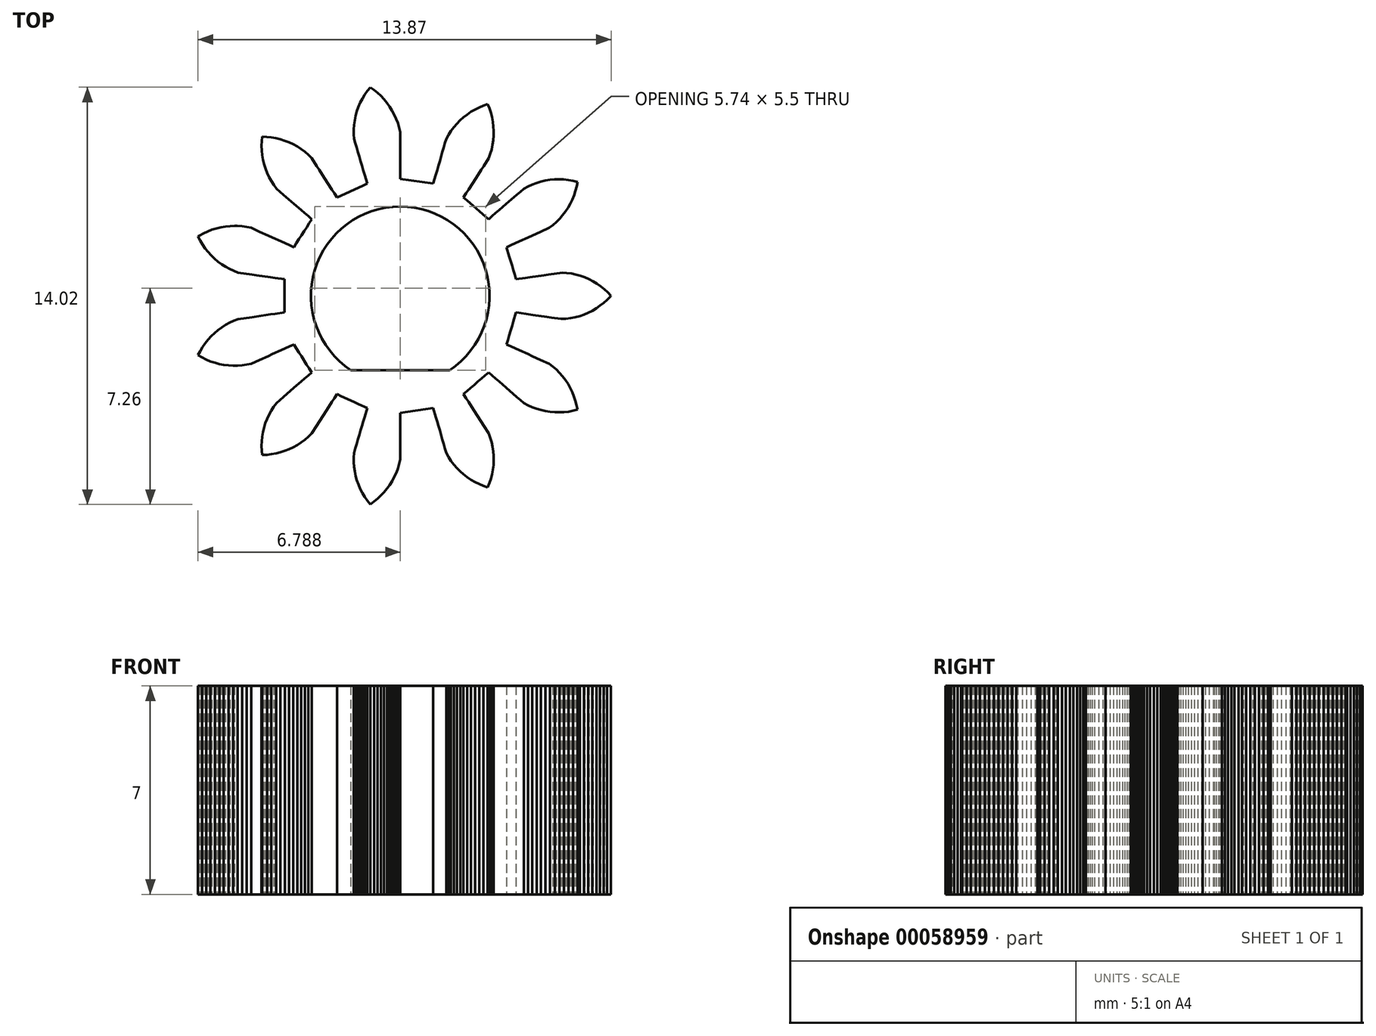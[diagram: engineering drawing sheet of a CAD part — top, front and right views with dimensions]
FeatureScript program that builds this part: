
annotation { "Feature Type Name" : "Feature", "Feature Type Description" : "" }
export const myFeature = defineFeature(function(context is Context, id is Id, definition is map)
    precondition{}
    {
        {
            var Q0;
            Q0=qCreatedBy(makeId("Top.planeOp"),FACE);
            var sketch = newSketch(context, id + "F0", { "sketchPlane" : qUnion([Q0])});
            skLineSegment(sketch, "E0", {"start": v(2.78, -0.56) * mm, "end": v(2.88, -0.57) * mm});
            skLineSegment(sketch, "E1", {"start": v(2.88, -0.57) * mm, "end": v(3.04, -0.6) * mm});
            skLineSegment(sketch, "E2", {"start": v(3.04, -0.6) * mm, "end": v(3.2, -0.62) * mm});
            skLineSegment(sketch, "E3", {"start": v(3.2, -0.62) * mm, "end": v(3.35, -0.64) * mm});
            skLineSegment(sketch, "E4", {"start": v(3.35, -0.64) * mm, "end": v(3.5, -0.66) * mm});
            skLineSegment(sketch, "E5", {"start": v(3.5, -0.66) * mm, "end": v(3.66, -0.69) * mm});
            skLineSegment(sketch, "E6", {"start": v(3.66, -0.69) * mm, "end": v(3.81, -0.7) * mm});
            skLineSegment(sketch, "E7", {"start": v(3.81, -0.7) * mm, "end": v(3.97, -0.73) * mm});
            skLineSegment(sketch, "E8", {"start": v(3.97, -0.73) * mm, "end": v(4.12, -0.75) * mm});
            skLineSegment(sketch, "E9", {"start": v(4.12, -0.75) * mm, "end": v(4.28, -0.78) * mm});
            skLineSegment(sketch, "E10", {"start": v(4.28, -0.78) * mm, "end": v(4.46, -0.77) * mm});
            skLineSegment(sketch, "E11", {"start": v(4.46, -0.77) * mm, "end": v(4.61, -0.75) * mm});
            skLineSegment(sketch, "E12", {"start": v(4.61, -0.75) * mm, "end": v(4.76, -0.72) * mm});
            skLineSegment(sketch, "E13", {"start": v(4.76, -0.72) * mm, "end": v(4.91, -0.68) * mm});
            skLineSegment(sketch, "E14", {"start": v(4.91, -0.68) * mm, "end": v(5.06, -0.63) * mm});
            skLineSegment(sketch, "E15", {"start": v(5.06, -0.63) * mm, "end": v(5.2, -0.57) * mm});
            skLineSegment(sketch, "E16", {"start": v(5.2, -0.57) * mm, "end": v(5.34, -0.5) * mm});
            skLineSegment(sketch, "E17", {"start": v(5.34, -0.5) * mm, "end": v(5.48, -0.42) * mm});
            skLineSegment(sketch, "E18", {"start": v(5.48, -0.42) * mm, "end": v(5.6, -0.33) * mm});
            skLineSegment(sketch, "E19", {"start": v(5.6, -0.33) * mm, "end": v(5.72, -0.23) * mm});
            skLineSegment(sketch, "E20", {"start": v(5.72, -0.23) * mm, "end": v(5.84, -0.13) * mm});
            skLineSegment(sketch, "E21", {"start": v(5.84, -0.13) * mm, "end": v(5.95, -0.02) * mm});
            skLineSegment(sketch, "E22", {"start": v(5.95, -0.02) * mm, "end": v(5.97, 0) * mm});
            skLineSegment(sketch, "E23", {"start": v(5.97, 0) * mm, "end": v(5.85, 0.12) * mm});
            skLineSegment(sketch, "E24", {"start": v(5.85, 0.12) * mm, "end": v(5.75, 0.22) * mm});
            skLineSegment(sketch, "E25", {"start": v(5.75, 0.22) * mm, "end": v(5.62, 0.32) * mm});
            skLineSegment(sketch, "E26", {"start": v(5.62, 0.32) * mm, "end": v(5.5, 0.4) * mm});
            skLineSegment(sketch, "E27", {"start": v(5.5, 0.4) * mm, "end": v(5.36, 0.49) * mm});
            skLineSegment(sketch, "E28", {"start": v(5.36, 0.49) * mm, "end": v(5.23, 0.56) * mm});
            skLineSegment(sketch, "E29", {"start": v(5.23, 0.56) * mm, "end": v(5.08, 0.62) * mm});
            skLineSegment(sketch, "E30", {"start": v(5.08, 0.62) * mm, "end": v(4.94, 0.67) * mm});
            skLineSegment(sketch, "E31", {"start": v(4.94, 0.67) * mm, "end": v(4.79, 0.72) * mm});
            skLineSegment(sketch, "E32", {"start": v(4.79, 0.72) * mm, "end": v(4.64, 0.75) * mm});
            skLineSegment(sketch, "E33", {"start": v(4.64, 0.75) * mm, "end": v(4.48, 0.77) * mm});
            skLineSegment(sketch, "E34", {"start": v(4.48, 0.77) * mm, "end": v(4.33, 0.78) * mm});
            skLineSegment(sketch, "E35", {"start": v(4.33, 0.78) * mm, "end": v(4.18, 0.76) * mm});
            skLineSegment(sketch, "E36", {"start": v(4.18, 0.76) * mm, "end": v(4.02, 0.74) * mm});
            skLineSegment(sketch, "E37", {"start": v(4.02, 0.74) * mm, "end": v(3.87, 0.72) * mm});
            skLineSegment(sketch, "E38", {"start": v(3.87, 0.72) * mm, "end": v(3.7, 0.7) * mm});
            skLineSegment(sketch, "E39", {"start": v(3.7, 0.7) * mm, "end": v(3.55, 0.67) * mm});
            skLineSegment(sketch, "E40", {"start": v(3.55, 0.67) * mm, "end": v(3.4, 0.65) * mm});
            skLineSegment(sketch, "E41", {"start": v(3.4, 0.65) * mm, "end": v(3.24, 0.63) * mm});
            skLineSegment(sketch, "E42", {"start": v(3.24, 0.63) * mm, "end": v(3.09, 0.6) * mm});
            skLineSegment(sketch, "E43", {"start": v(3.09, 0.6) * mm, "end": v(2.93, 0.58) * mm});
            skLineSegment(sketch, "E44", {"start": v(2.93, 0.58) * mm, "end": v(2.78, 0.56) * mm});
            skLineSegment(sketch, "E45", {"start": v(2.78, 0.56) * mm, "end": v(2.73, 0.71) * mm});
            skLineSegment(sketch, "E46", {"start": v(2.73, 0.71) * mm, "end": v(2.69, 0.87) * mm});
            skLineSegment(sketch, "E47", {"start": v(2.69, 0.87) * mm, "end": v(2.64, 1.02) * mm});
            skLineSegment(sketch, "E48", {"start": v(2.64, 1.02) * mm, "end": v(2.6, 1.17) * mm});
            skLineSegment(sketch, "E49", {"start": v(2.6, 1.17) * mm, "end": v(2.55, 1.33) * mm});
            skLineSegment(sketch, "E50", {"start": v(2.55, 1.33) * mm, "end": v(2.5, 1.48) * mm});
            skLineSegment(sketch, "E51", {"start": v(2.5, 1.48) * mm, "end": v(2.46, 1.63) * mm});
            skLineSegment(sketch, "E52", {"start": v(2.46, 1.63) * mm, "end": v(2.6, 1.7) * mm});
            skLineSegment(sketch, "E53", {"start": v(2.6, 1.7) * mm, "end": v(2.75, 1.76) * mm});
            skLineSegment(sketch, "E54", {"start": v(2.75, 1.76) * mm, "end": v(2.9, 1.83) * mm});
            skLineSegment(sketch, "E55", {"start": v(2.9, 1.83) * mm, "end": v(3.03, 1.9) * mm});
            skLineSegment(sketch, "E56", {"start": v(3.03, 1.9) * mm, "end": v(3.18, 1.96) * mm});
            skLineSegment(sketch, "E57", {"start": v(3.18, 1.96) * mm, "end": v(3.32, 2.02) * mm});
            skLineSegment(sketch, "E58", {"start": v(3.32, 2.02) * mm, "end": v(3.46, 2.09) * mm});
            skLineSegment(sketch, "E59", {"start": v(3.46, 2.09) * mm, "end": v(3.6, 2.15) * mm});
            skLineSegment(sketch, "E60", {"start": v(3.6, 2.15) * mm, "end": v(3.75, 2.22) * mm});
            skLineSegment(sketch, "E61", {"start": v(3.75, 2.22) * mm, "end": v(3.9, 2.28) * mm});
            skLineSegment(sketch, "E62", {"start": v(3.9, 2.28) * mm, "end": v(4.02, 2.38) * mm});
            skLineSegment(sketch, "E63", {"start": v(4.02, 2.38) * mm, "end": v(4.13, 2.48) * mm});
            skLineSegment(sketch, "E64", {"start": v(4.13, 2.48) * mm, "end": v(4.24, 2.6) * mm});
            skLineSegment(sketch, "E65", {"start": v(4.24, 2.6) * mm, "end": v(4.34, 2.7) * mm});
            skLineSegment(sketch, "E66", {"start": v(4.34, 2.7) * mm, "end": v(4.44, 2.83) * mm});
            skLineSegment(sketch, "E67", {"start": v(4.44, 2.83) * mm, "end": v(4.52, 2.96) * mm});
            skLineSegment(sketch, "E68", {"start": v(4.52, 2.96) * mm, "end": v(4.6, 3.1) * mm});
            skLineSegment(sketch, "E69", {"start": v(4.6, 3.1) * mm, "end": v(4.67, 3.23) * mm});
            skLineSegment(sketch, "E70", {"start": v(4.67, 3.23) * mm, "end": v(4.73, 3.38) * mm});
            skLineSegment(sketch, "E71", {"start": v(4.73, 3.38) * mm, "end": v(4.77, 3.52) * mm});
            skLineSegment(sketch, "E72", {"start": v(4.77, 3.52) * mm, "end": v(4.81, 3.68) * mm});
            skLineSegment(sketch, "E73", {"start": v(4.81, 3.68) * mm, "end": v(4.84, 3.83) * mm});
            skLineSegment(sketch, "E74", {"start": v(4.84, 3.83) * mm, "end": v(4.69, 3.86) * mm});
            skLineSegment(sketch, "E75", {"start": v(4.69, 3.86) * mm, "end": v(4.54, 3.9) * mm});
            skLineSegment(sketch, "E76", {"start": v(4.54, 3.9) * mm, "end": v(4.38, 3.9) * mm});
            skLineSegment(sketch, "E77", {"start": v(4.38, 3.9) * mm, "end": v(4.23, 3.91) * mm});
            skLineSegment(sketch, "E78", {"start": v(4.23, 3.91) * mm, "end": v(4.07, 3.9) * mm});
            skLineSegment(sketch, "E79", {"start": v(4.07, 3.9) * mm, "end": v(3.92, 3.9) * mm});
            skLineSegment(sketch, "E80", {"start": v(3.92, 3.9) * mm, "end": v(3.76, 3.87) * mm});
            skLineSegment(sketch, "E81", {"start": v(3.76, 3.87) * mm, "end": v(3.62, 3.84) * mm});
            skLineSegment(sketch, "E82", {"start": v(3.62, 3.84) * mm, "end": v(3.46, 3.8) * mm});
            skLineSegment(sketch, "E83", {"start": v(3.46, 3.8) * mm, "end": v(3.32, 3.74) * mm});
            skLineSegment(sketch, "E84", {"start": v(3.32, 3.74) * mm, "end": v(3.18, 3.67) * mm});
            skLineSegment(sketch, "E85", {"start": v(3.18, 3.67) * mm, "end": v(3.04, 3.6) * mm});
            skLineSegment(sketch, "E86", {"start": v(3.04, 3.6) * mm, "end": v(2.93, 3.5) * mm});
            skLineSegment(sketch, "E87", {"start": v(2.93, 3.5) * mm, "end": v(2.8, 3.4) * mm});
            skLineSegment(sketch, "E88", {"start": v(2.8, 3.4) * mm, "end": v(2.69, 3.3) * mm});
            skLineSegment(sketch, "E89", {"start": v(2.69, 3.3) * mm, "end": v(2.57, 3.2) * mm});
            skLineSegment(sketch, "E90", {"start": v(2.57, 3.2) * mm, "end": v(2.45, 3.09) * mm});
            skLineSegment(sketch, "E91", {"start": v(2.45, 3.09) * mm, "end": v(2.33, 2.98) * mm});
            skLineSegment(sketch, "E92", {"start": v(2.33, 2.98) * mm, "end": v(2.21, 2.88) * mm});
            skLineSegment(sketch, "E93", {"start": v(2.21, 2.88) * mm, "end": v(2.1, 2.78) * mm});
            skLineSegment(sketch, "E94", {"start": v(2.1, 2.78) * mm, "end": v(1.98, 2.68) * mm});
            skLineSegment(sketch, "E95", {"start": v(1.98, 2.68) * mm, "end": v(1.86, 2.57) * mm});
            skLineSegment(sketch, "E96", {"start": v(1.86, 2.57) * mm, "end": v(1.74, 2.68) * mm});
            skLineSegment(sketch, "E97", {"start": v(1.74, 2.68) * mm, "end": v(1.62, 2.78) * mm});
            skLineSegment(sketch, "E98", {"start": v(1.62, 2.78) * mm, "end": v(1.5, 2.89) * mm});
            skLineSegment(sketch, "E99", {"start": v(1.5, 2.89) * mm, "end": v(1.37, 3) * mm});
            skLineSegment(sketch, "E100", {"start": v(1.37, 3) * mm, "end": v(1.25, 3.1) * mm});
            skLineSegment(sketch, "E101", {"start": v(1.25, 3.1) * mm, "end": v(1.13, 3.2) * mm});
            skLineSegment(sketch, "E102", {"start": v(1.13, 3.2) * mm, "end": v(1.01, 3.3) * mm});
            skLineSegment(sketch, "E103", {"start": v(1.01, 3.3) * mm, "end": v(1.1, 3.44) * mm});
            skLineSegment(sketch, "E104", {"start": v(1.1, 3.44) * mm, "end": v(1.18, 3.57) * mm});
            skLineSegment(sketch, "E105", {"start": v(1.18, 3.57) * mm, "end": v(1.27, 3.7) * mm});
            skLineSegment(sketch, "E106", {"start": v(1.27, 3.7) * mm, "end": v(1.35, 3.83) * mm});
            skLineSegment(sketch, "E107", {"start": v(1.35, 3.83) * mm, "end": v(1.44, 3.97) * mm});
            skLineSegment(sketch, "E108", {"start": v(1.44, 3.97) * mm, "end": v(1.52, 4.1) * mm});
            skLineSegment(sketch, "E109", {"start": v(1.52, 4.1) * mm, "end": v(1.6, 4.23) * mm});
            skLineSegment(sketch, "E110", {"start": v(1.6, 4.23) * mm, "end": v(1.7, 4.36) * mm});
            skLineSegment(sketch, "E111", {"start": v(1.7, 4.36) * mm, "end": v(1.78, 4.5) * mm});
            skLineSegment(sketch, "E112", {"start": v(1.78, 4.5) * mm, "end": v(1.86, 4.63) * mm});
            skLineSegment(sketch, "E113", {"start": v(1.86, 4.63) * mm, "end": v(1.91, 4.78) * mm});
            skLineSegment(sketch, "E114", {"start": v(1.91, 4.78) * mm, "end": v(1.96, 4.92) * mm});
            skLineSegment(sketch, "E115", {"start": v(1.96, 4.92) * mm, "end": v(2, 5.08) * mm});
            skLineSegment(sketch, "E116", {"start": v(2, 5.08) * mm, "end": v(2.01, 5.23) * mm});
            skLineSegment(sketch, "E117", {"start": v(2.01, 5.23) * mm, "end": v(2.03, 5.39) * mm});
            skLineSegment(sketch, "E118", {"start": v(2.03, 5.39) * mm, "end": v(2.03, 5.54) * mm});
            skLineSegment(sketch, "E119", {"start": v(2.03, 5.54) * mm, "end": v(2.02, 5.7) * mm});
            skLineSegment(sketch, "E120", {"start": v(2.02, 5.7) * mm, "end": v(2, 5.84) * mm});
            skLineSegment(sketch, "E121", {"start": v(2, 5.84) * mm, "end": v(1.97, 6) * mm});
            skLineSegment(sketch, "E122", {"start": v(1.97, 6) * mm, "end": v(1.93, 6.15) * mm});
            skLineSegment(sketch, "E123", {"start": v(1.93, 6.15) * mm, "end": v(1.88, 6.3) * mm});
            skLineSegment(sketch, "E124", {"start": v(1.88, 6.3) * mm, "end": v(1.83, 6.44) * mm});
            skLineSegment(sketch, "E125", {"start": v(1.83, 6.44) * mm, "end": v(1.68, 6.39) * mm});
            skLineSegment(sketch, "E126", {"start": v(1.68, 6.39) * mm, "end": v(1.54, 6.33) * mm});
            skLineSegment(sketch, "E127", {"start": v(1.54, 6.33) * mm, "end": v(1.4, 6.26) * mm});
            skLineSegment(sketch, "E128", {"start": v(1.4, 6.26) * mm, "end": v(1.27, 6.18) * mm});
            skLineSegment(sketch, "E129", {"start": v(1.27, 6.18) * mm, "end": v(1.13, 6.1) * mm});
            skLineSegment(sketch, "E130", {"start": v(1.13, 6.1) * mm, "end": v(1.01, 6) * mm});
            skLineSegment(sketch, "E131", {"start": v(1.01, 6) * mm, "end": v(0.9, 5.9) * mm});
            skLineSegment(sketch, "E132", {"start": v(0.9, 5.9) * mm, "end": v(0.8, 5.78) * mm});
            skLineSegment(sketch, "E133", {"start": v(0.8, 5.78) * mm, "end": v(0.69, 5.66) * mm});
            skLineSegment(sketch, "E134", {"start": v(0.69, 5.66) * mm, "end": v(0.6, 5.54) * mm});
            skLineSegment(sketch, "E135", {"start": v(0.6, 5.54) * mm, "end": v(0.51, 5.4) * mm});
            skLineSegment(sketch, "E136", {"start": v(0.51, 5.4) * mm, "end": v(0.44, 5.28) * mm});
            skLineSegment(sketch, "E137", {"start": v(0.44, 5.28) * mm, "end": v(0.4, 5.13) * mm});
            skLineSegment(sketch, "E138", {"start": v(0.4, 5.13) * mm, "end": v(0.35, 4.98) * mm});
            skLineSegment(sketch, "E139", {"start": v(0.35, 4.98) * mm, "end": v(0.3, 4.83) * mm});
            skLineSegment(sketch, "E140", {"start": v(0.3, 4.83) * mm, "end": v(0.26, 4.67) * mm});
            skLineSegment(sketch, "E141", {"start": v(0.26, 4.67) * mm, "end": v(0.22, 4.52) * mm});
            skLineSegment(sketch, "E142", {"start": v(0.22, 4.52) * mm, "end": v(0.17, 4.37) * mm});
            skLineSegment(sketch, "E143", {"start": v(0.17, 4.37) * mm, "end": v(0.13, 4.22) * mm});
            skLineSegment(sketch, "E144", {"start": v(0.13, 4.22) * mm, "end": v(0.08, 4.07) * mm});
            skLineSegment(sketch, "E145", {"start": v(0.08, 4.07) * mm, "end": v(0.04, 3.92) * mm});
            skLineSegment(sketch, "E146", {"start": v(0.04, 3.92) * mm, "end": v(0, 3.77) * mm});
            skLineSegment(sketch, "E147", {"start": v(0, 3.77) * mm, "end": v(-0.16, 3.8) * mm});
            skLineSegment(sketch, "E148", {"start": v(-0.16, 3.8) * mm, "end": v(-0.32, 3.82) * mm});
            skLineSegment(sketch, "E149", {"start": v(-0.32, 3.82) * mm, "end": v(-0.48, 3.84) * mm});
            skLineSegment(sketch, "E150", {"start": v(-0.48, 3.84) * mm, "end": v(-0.64, 3.86) * mm});
            skLineSegment(sketch, "E151", {"start": v(-0.64, 3.86) * mm, "end": v(-0.8, 3.88) * mm});
            skLineSegment(sketch, "E152", {"start": v(-0.8, 3.88) * mm, "end": v(-0.95, 3.9) * mm});
            skLineSegment(sketch, "E153", {"start": v(-0.95, 3.9) * mm, "end": v(-1.11, 3.93) * mm});
            skLineSegment(sketch, "E154", {"start": v(-1.11, 3.93) * mm, "end": v(-1.11, 4.09) * mm});
            skLineSegment(sketch, "E155", {"start": v(-1.11, 4.09) * mm, "end": v(-1.11, 4.24) * mm});
            skLineSegment(sketch, "E156", {"start": v(-1.11, 4.24) * mm, "end": v(-1.11, 4.4) * mm});
            skLineSegment(sketch, "E157", {"start": v(-1.11, 4.4) * mm, "end": v(-1.11, 4.56) * mm});
            skLineSegment(sketch, "E158", {"start": v(-1.11, 4.56) * mm, "end": v(-1.11, 4.71) * mm});
            skLineSegment(sketch, "E159", {"start": v(-1.11, 4.71) * mm, "end": v(-1.11, 4.87) * mm});
            skLineSegment(sketch, "E160", {"start": v(-1.11, 4.87) * mm, "end": v(-1.11, 5.03) * mm});
            skLineSegment(sketch, "E161", {"start": v(-1.11, 5.03) * mm, "end": v(-1.11, 5.19) * mm});
            skLineSegment(sketch, "E162", {"start": v(-1.11, 5.19) * mm, "end": v(-1.11, 5.34) * mm});
            skLineSegment(sketch, "E163", {"start": v(-1.11, 5.34) * mm, "end": v(-1.11, 5.5) * mm});
            skLineSegment(sketch, "E164", {"start": v(-1.11, 5.5) * mm, "end": v(-1.15, 5.66) * mm});
            skLineSegment(sketch, "E165", {"start": v(-1.15, 5.66) * mm, "end": v(-1.2, 5.8) * mm});
            skLineSegment(sketch, "E166", {"start": v(-1.2, 5.8) * mm, "end": v(-1.25, 5.95) * mm});
            skLineSegment(sketch, "E167", {"start": v(-1.25, 5.95) * mm, "end": v(-1.3, 6.09) * mm});
            skLineSegment(sketch, "E168", {"start": v(-1.3, 6.09) * mm, "end": v(-1.38, 6.23) * mm});
            skLineSegment(sketch, "E169", {"start": v(-1.38, 6.23) * mm, "end": v(-1.46, 6.36) * mm});
            skLineSegment(sketch, "E170", {"start": v(-1.46, 6.36) * mm, "end": v(-1.56, 6.48) * mm});
            skLineSegment(sketch, "E171", {"start": v(-1.56, 6.48) * mm, "end": v(-1.65, 6.6) * mm});
            skLineSegment(sketch, "E172", {"start": v(-1.65, 6.6) * mm, "end": v(-1.76, 6.72) * mm});
            skLineSegment(sketch, "E173", {"start": v(-1.76, 6.72) * mm, "end": v(-1.87, 6.82) * mm});
            skLineSegment(sketch, "E174", {"start": v(-1.87, 6.82) * mm, "end": v(-2, 6.92) * mm});
            skLineSegment(sketch, "E175", {"start": v(-2, 6.92) * mm, "end": v(-2.12, 7) * mm});
            skLineSegment(sketch, "E176", {"start": v(-2.12, 7) * mm, "end": v(-2.22, 6.88) * mm});
            skLineSegment(sketch, "E177", {"start": v(-2.22, 6.88) * mm, "end": v(-2.3, 6.76) * mm});
            skLineSegment(sketch, "E178", {"start": v(-2.3, 6.76) * mm, "end": v(-2.38, 6.62) * mm});
            skLineSegment(sketch, "E179", {"start": v(-2.38, 6.62) * mm, "end": v(-2.45, 6.49) * mm});
            skLineSegment(sketch, "E180", {"start": v(-2.45, 6.49) * mm, "end": v(-2.52, 6.34) * mm});
            skLineSegment(sketch, "E181", {"start": v(-2.52, 6.34) * mm, "end": v(-2.57, 6.2) * mm});
            skLineSegment(sketch, "E182", {"start": v(-2.57, 6.2) * mm, "end": v(-2.6, 6.04) * mm});
            skLineSegment(sketch, "E183", {"start": v(-2.6, 6.04) * mm, "end": v(-2.64, 5.9) * mm});
            skLineSegment(sketch, "E184", {"start": v(-2.64, 5.9) * mm, "end": v(-2.66, 5.74) * mm});
            skLineSegment(sketch, "E185", {"start": v(-2.66, 5.74) * mm, "end": v(-2.67, 5.59) * mm});
            skLineSegment(sketch, "E186", {"start": v(-2.67, 5.59) * mm, "end": v(-2.67, 5.43) * mm});
            skLineSegment(sketch, "E187", {"start": v(-2.67, 5.43) * mm, "end": v(-2.66, 5.28) * mm});
            skLineSegment(sketch, "E188", {"start": v(-2.66, 5.28) * mm, "end": v(-2.62, 5.13) * mm});
            skLineSegment(sketch, "E189", {"start": v(-2.62, 5.13) * mm, "end": v(-2.57, 4.98) * mm});
            skLineSegment(sketch, "E190", {"start": v(-2.57, 4.98) * mm, "end": v(-2.53, 4.83) * mm});
            skLineSegment(sketch, "E191", {"start": v(-2.53, 4.83) * mm, "end": v(-2.48, 4.67) * mm});
            skLineSegment(sketch, "E192", {"start": v(-2.48, 4.67) * mm, "end": v(-2.44, 4.52) * mm});
            skLineSegment(sketch, "E193", {"start": v(-2.44, 4.52) * mm, "end": v(-2.4, 4.37) * mm});
            skLineSegment(sketch, "E194", {"start": v(-2.4, 4.37) * mm, "end": v(-2.35, 4.22) * mm});
            skLineSegment(sketch, "E195", {"start": v(-2.35, 4.22) * mm, "end": v(-2.3, 4.07) * mm});
            skLineSegment(sketch, "E196", {"start": v(-2.3, 4.07) * mm, "end": v(-2.26, 3.92) * mm});
            skLineSegment(sketch, "E197", {"start": v(-2.26, 3.92) * mm, "end": v(-2.22, 3.77) * mm});
            skLineSegment(sketch, "E198", {"start": v(-2.22, 3.77) * mm, "end": v(-2.36, 3.7) * mm});
            skLineSegment(sketch, "E199", {"start": v(-2.36, 3.7) * mm, "end": v(-2.5, 3.64) * mm});
            skLineSegment(sketch, "E200", {"start": v(-2.5, 3.64) * mm, "end": v(-2.66, 3.57) * mm});
            skLineSegment(sketch, "E201", {"start": v(-2.66, 3.57) * mm, "end": v(-2.8, 3.5) * mm});
            skLineSegment(sketch, "E202", {"start": v(-2.8, 3.5) * mm, "end": v(-2.95, 3.44) * mm});
            skLineSegment(sketch, "E203", {"start": v(-2.95, 3.44) * mm, "end": v(-3.1, 3.37) * mm});
            skLineSegment(sketch, "E204", {"start": v(-3.1, 3.37) * mm, "end": v(-3.24, 3.3) * mm});
            skLineSegment(sketch, "E205", {"start": v(-3.24, 3.3) * mm, "end": v(-3.32, 3.44) * mm});
            skLineSegment(sketch, "E206", {"start": v(-3.32, 3.44) * mm, "end": v(-3.4, 3.57) * mm});
            skLineSegment(sketch, "E207", {"start": v(-3.4, 3.57) * mm, "end": v(-3.5, 3.7) * mm});
            skLineSegment(sketch, "E208", {"start": v(-3.5, 3.7) * mm, "end": v(-3.58, 3.83) * mm});
            skLineSegment(sketch, "E209", {"start": v(-3.58, 3.83) * mm, "end": v(-3.66, 3.97) * mm});
            skLineSegment(sketch, "E210", {"start": v(-3.66, 3.97) * mm, "end": v(-3.75, 4.1) * mm});
            skLineSegment(sketch, "E211", {"start": v(-3.75, 4.1) * mm, "end": v(-3.83, 4.23) * mm});
            skLineSegment(sketch, "E212", {"start": v(-3.83, 4.23) * mm, "end": v(-3.92, 4.36) * mm});
            skLineSegment(sketch, "E213", {"start": v(-3.92, 4.36) * mm, "end": v(-4, 4.5) * mm});
            skLineSegment(sketch, "E214", {"start": v(-4, 4.5) * mm, "end": v(-4.09, 4.63) * mm});
            skLineSegment(sketch, "E215", {"start": v(-4.09, 4.63) * mm, "end": v(-4.2, 4.74) * mm});
            skLineSegment(sketch, "E216", {"start": v(-4.2, 4.74) * mm, "end": v(-4.31, 4.84) * mm});
            skLineSegment(sketch, "E217", {"start": v(-4.31, 4.84) * mm, "end": v(-4.44, 4.93) * mm});
            skLineSegment(sketch, "E218", {"start": v(-4.44, 4.93) * mm, "end": v(-4.57, 5.01) * mm});
            skLineSegment(sketch, "E219", {"start": v(-4.57, 5.01) * mm, "end": v(-4.7, 5.1) * mm});
            skLineSegment(sketch, "E220", {"start": v(-4.7, 5.1) * mm, "end": v(-4.84, 5.16) * mm});
            skLineSegment(sketch, "E221", {"start": v(-4.84, 5.16) * mm, "end": v(-5, 5.21) * mm});
            skLineSegment(sketch, "E222", {"start": v(-5, 5.21) * mm, "end": v(-5.14, 5.26) * mm});
            skLineSegment(sketch, "E223", {"start": v(-5.14, 5.26) * mm, "end": v(-5.3, 5.3) * mm});
            skLineSegment(sketch, "E224", {"start": v(-5.3, 5.3) * mm, "end": v(-5.44, 5.33) * mm});
            skLineSegment(sketch, "E225", {"start": v(-5.44, 5.33) * mm, "end": v(-5.6, 5.34) * mm});
            skLineSegment(sketch, "E226", {"start": v(-5.6, 5.34) * mm, "end": v(-5.75, 5.35) * mm});
            skLineSegment(sketch, "E227", {"start": v(-5.75, 5.35) * mm, "end": v(-5.76, 5.2) * mm});
            skLineSegment(sketch, "E228", {"start": v(-5.76, 5.2) * mm, "end": v(-5.77, 5.04) * mm});
            skLineSegment(sketch, "E229", {"start": v(-5.77, 5.04) * mm, "end": v(-5.76, 4.88) * mm});
            skLineSegment(sketch, "E230", {"start": v(-5.76, 4.88) * mm, "end": v(-5.75, 4.73) * mm});
            skLineSegment(sketch, "E231", {"start": v(-5.75, 4.73) * mm, "end": v(-5.72, 4.57) * mm});
            skLineSegment(sketch, "E232", {"start": v(-5.72, 4.57) * mm, "end": v(-5.69, 4.43) * mm});
            skLineSegment(sketch, "E233", {"start": v(-5.69, 4.43) * mm, "end": v(-5.64, 4.27) * mm});
            skLineSegment(sketch, "E234", {"start": v(-5.64, 4.27) * mm, "end": v(-5.58, 4.13) * mm});
            skLineSegment(sketch, "E235", {"start": v(-5.58, 4.13) * mm, "end": v(-5.52, 3.99) * mm});
            skLineSegment(sketch, "E236", {"start": v(-5.52, 3.99) * mm, "end": v(-5.44, 3.86) * mm});
            skLineSegment(sketch, "E237", {"start": v(-5.44, 3.86) * mm, "end": v(-5.36, 3.72) * mm});
            skLineSegment(sketch, "E238", {"start": v(-5.36, 3.72) * mm, "end": v(-5.27, 3.6) * mm});
            skLineSegment(sketch, "E239", {"start": v(-5.27, 3.6) * mm, "end": v(-5.15, 3.5) * mm});
            skLineSegment(sketch, "E240", {"start": v(-5.15, 3.5) * mm, "end": v(-5.03, 3.4) * mm});
            skLineSegment(sketch, "E241", {"start": v(-5.03, 3.4) * mm, "end": v(-4.91, 3.3) * mm});
            skLineSegment(sketch, "E242", {"start": v(-4.91, 3.3) * mm, "end": v(-4.8, 3.2) * mm});
            skLineSegment(sketch, "E243", {"start": v(-4.8, 3.2) * mm, "end": v(-4.68, 3.09) * mm});
            skLineSegment(sketch, "E244", {"start": v(-4.68, 3.09) * mm, "end": v(-4.56, 2.98) * mm});
            skLineSegment(sketch, "E245", {"start": v(-4.56, 2.98) * mm, "end": v(-4.44, 2.88) * mm});
            skLineSegment(sketch, "E246", {"start": v(-4.44, 2.88) * mm, "end": v(-4.32, 2.78) * mm});
            skLineSegment(sketch, "E247", {"start": v(-4.32, 2.78) * mm, "end": v(-4.2, 2.68) * mm});
            skLineSegment(sketch, "E248", {"start": v(-4.2, 2.68) * mm, "end": v(-4.08, 2.57) * mm});
            skLineSegment(sketch, "E249", {"start": v(-4.08, 2.57) * mm, "end": v(-4.17, 2.44) * mm});
            skLineSegment(sketch, "E250", {"start": v(-4.17, 2.44) * mm, "end": v(-4.25, 2.3) * mm});
            skLineSegment(sketch, "E251", {"start": v(-4.25, 2.3) * mm, "end": v(-4.34, 2.17) * mm});
            skLineSegment(sketch, "E252", {"start": v(-4.34, 2.17) * mm, "end": v(-4.43, 2.04) * mm});
            skLineSegment(sketch, "E253", {"start": v(-4.43, 2.04) * mm, "end": v(-4.51, 1.9) * mm});
            skLineSegment(sketch, "E254", {"start": v(-4.51, 1.9) * mm, "end": v(-4.6, 1.77) * mm});
            skLineSegment(sketch, "E255", {"start": v(-4.6, 1.77) * mm, "end": v(-4.69, 1.63) * mm});
            skLineSegment(sketch, "E256", {"start": v(-4.69, 1.63) * mm, "end": v(-4.83, 1.7) * mm});
            skLineSegment(sketch, "E257", {"start": v(-4.83, 1.7) * mm, "end": v(-4.97, 1.76) * mm});
            skLineSegment(sketch, "E258", {"start": v(-4.97, 1.76) * mm, "end": v(-5.12, 1.83) * mm});
            skLineSegment(sketch, "E259", {"start": v(-5.12, 1.83) * mm, "end": v(-5.26, 1.9) * mm});
            skLineSegment(sketch, "E260", {"start": v(-5.26, 1.9) * mm, "end": v(-5.4, 1.96) * mm});
            skLineSegment(sketch, "E261", {"start": v(-5.4, 1.96) * mm, "end": v(-5.54, 2.02) * mm});
            skLineSegment(sketch, "E262", {"start": v(-5.54, 2.02) * mm, "end": v(-5.69, 2.09) * mm});
            skLineSegment(sketch, "E263", {"start": v(-5.69, 2.09) * mm, "end": v(-5.83, 2.15) * mm});
            skLineSegment(sketch, "E264", {"start": v(-5.83, 2.15) * mm, "end": v(-5.97, 2.22) * mm});
            skLineSegment(sketch, "E265", {"start": v(-5.97, 2.22) * mm, "end": v(-6.12, 2.28) * mm});
            skLineSegment(sketch, "E266", {"start": v(-6.12, 2.28) * mm, "end": v(-6.27, 2.32) * mm});
            skLineSegment(sketch, "E267", {"start": v(-6.27, 2.32) * mm, "end": v(-6.42, 2.34) * mm});
            skLineSegment(sketch, "E268", {"start": v(-6.42, 2.34) * mm, "end": v(-6.58, 2.35) * mm});
            skLineSegment(sketch, "E269", {"start": v(-6.58, 2.35) * mm, "end": v(-6.67, 2.35) * mm});
            skLineSegment(sketch, "E270", {"start": v(-6.67, 2.35) * mm, "end": v(-6.83, 2.34) * mm});
            skLineSegment(sketch, "E271", {"start": v(-6.83, 2.34) * mm, "end": v(-6.98, 2.33) * mm});
            skLineSegment(sketch, "E272", {"start": v(-6.98, 2.33) * mm, "end": v(-7.13, 2.3) * mm});
            skLineSegment(sketch, "E273", {"start": v(-7.13, 2.3) * mm, "end": v(-7.28, 2.27) * mm});
            skLineSegment(sketch, "E274", {"start": v(-7.28, 2.27) * mm, "end": v(-7.43, 2.22) * mm});
            skLineSegment(sketch, "E275", {"start": v(-7.43, 2.22) * mm, "end": v(-7.57, 2.17) * mm});
            skLineSegment(sketch, "E276", {"start": v(-7.57, 2.17) * mm, "end": v(-7.72, 2.1) * mm});
            skLineSegment(sketch, "E277", {"start": v(-7.72, 2.1) * mm, "end": v(-7.85, 2.03) * mm});
            skLineSegment(sketch, "E278", {"start": v(-7.85, 2.03) * mm, "end": v(-7.9, 2) * mm});
            skLineSegment(sketch, "E279", {"start": v(-7.9, 2) * mm, "end": v(-7.83, 1.85) * mm});
            skLineSegment(sketch, "E280", {"start": v(-7.83, 1.85) * mm, "end": v(-7.75, 1.72) * mm});
            skLineSegment(sketch, "E281", {"start": v(-7.75, 1.72) * mm, "end": v(-7.66, 1.6) * mm});
            skLineSegment(sketch, "E282", {"start": v(-7.66, 1.6) * mm, "end": v(-7.57, 1.47) * mm});
            skLineSegment(sketch, "E283", {"start": v(-7.57, 1.47) * mm, "end": v(-7.46, 1.36) * mm});
            skLineSegment(sketch, "E284", {"start": v(-7.46, 1.36) * mm, "end": v(-7.35, 1.25) * mm});
            skLineSegment(sketch, "E285", {"start": v(-7.35, 1.25) * mm, "end": v(-7.23, 1.15) * mm});
            skLineSegment(sketch, "E286", {"start": v(-7.23, 1.15) * mm, "end": v(-7.1, 1.06) * mm});
            skLineSegment(sketch, "E287", {"start": v(-7.1, 1.06) * mm, "end": v(-6.97, 0.98) * mm});
            skLineSegment(sketch, "E288", {"start": v(-6.97, 0.98) * mm, "end": v(-6.84, 0.9) * mm});
            skLineSegment(sketch, "E289", {"start": v(-6.84, 0.9) * mm, "end": v(-6.7, 0.84) * mm});
            skLineSegment(sketch, "E290", {"start": v(-6.7, 0.84) * mm, "end": v(-6.56, 0.78) * mm});
            skLineSegment(sketch, "E291", {"start": v(-6.56, 0.78) * mm, "end": v(-6.4, 0.76) * mm});
            skLineSegment(sketch, "E292", {"start": v(-6.4, 0.76) * mm, "end": v(-6.25, 0.74) * mm});
            skLineSegment(sketch, "E293", {"start": v(-6.25, 0.74) * mm, "end": v(-6.1, 0.72) * mm});
            skLineSegment(sketch, "E294", {"start": v(-6.1, 0.72) * mm, "end": v(-5.93, 0.7) * mm});
            skLineSegment(sketch, "E295", {"start": v(-5.93, 0.7) * mm, "end": v(-5.78, 0.67) * mm});
            skLineSegment(sketch, "E296", {"start": v(-5.78, 0.67) * mm, "end": v(-5.62, 0.65) * mm});
            skLineSegment(sketch, "E297", {"start": v(-5.62, 0.65) * mm, "end": v(-5.47, 0.63) * mm});
            skLineSegment(sketch, "E298", {"start": v(-5.47, 0.63) * mm, "end": v(-5.31, 0.6) * mm});
            skLineSegment(sketch, "E299", {"start": v(-5.31, 0.6) * mm, "end": v(-5.16, 0.58) * mm});
            skLineSegment(sketch, "E300", {"start": v(-5.16, 0.58) * mm, "end": v(-5, 0.56) * mm});
            skLineSegment(sketch, "E301", {"start": v(-5, 0.56) * mm, "end": v(-5, 0.4) * mm});
            skLineSegment(sketch, "E302", {"start": v(-5, 0.4) * mm, "end": v(-5, 0.24) * mm});
            skLineSegment(sketch, "E303", {"start": v(-5, 0.24) * mm, "end": v(-5, 0.08) * mm});
            skLineSegment(sketch, "E304", {"start": v(-5, 0.08) * mm, "end": v(-5, -0.08) * mm});
            skLineSegment(sketch, "E305", {"start": v(-5, -0.08) * mm, "end": v(-5, -0.24) * mm});
            skLineSegment(sketch, "E306", {"start": v(-5, -0.24) * mm, "end": v(-5, -0.4) * mm});
            skLineSegment(sketch, "E307", {"start": v(-5, -0.4) * mm, "end": v(-5, -0.56) * mm});
            skLineSegment(sketch, "E308", {"start": v(-5, -0.56) * mm, "end": v(-5.16, -0.58) * mm});
            skLineSegment(sketch, "E309", {"start": v(-5.16, -0.58) * mm, "end": v(-5.31, -0.6) * mm});
            skLineSegment(sketch, "E310", {"start": v(-5.31, -0.6) * mm, "end": v(-5.47, -0.63) * mm});
            skLineSegment(sketch, "E311", {"start": v(-5.47, -0.63) * mm, "end": v(-5.62, -0.65) * mm});
            skLineSegment(sketch, "E312", {"start": v(-5.62, -0.65) * mm, "end": v(-5.78, -0.67) * mm});
            skLineSegment(sketch, "E313", {"start": v(-5.78, -0.67) * mm, "end": v(-5.93, -0.7) * mm});
            skLineSegment(sketch, "E314", {"start": v(-5.93, -0.7) * mm, "end": v(-6.1, -0.72) * mm});
            skLineSegment(sketch, "E315", {"start": v(-6.1, -0.72) * mm, "end": v(-6.25, -0.74) * mm});
            skLineSegment(sketch, "E316", {"start": v(-6.25, -0.74) * mm, "end": v(-6.4, -0.76) * mm});
            skLineSegment(sketch, "E317", {"start": v(-6.4, -0.76) * mm, "end": v(-6.56, -0.78) * mm});
            skLineSegment(sketch, "E318", {"start": v(-6.56, -0.78) * mm, "end": v(-6.7, -0.84) * mm});
            skLineSegment(sketch, "E319", {"start": v(-6.7, -0.84) * mm, "end": v(-6.84, -0.9) * mm});
            skLineSegment(sketch, "E320", {"start": v(-6.84, -0.9) * mm, "end": v(-6.98, -0.98) * mm});
            skLineSegment(sketch, "E321", {"start": v(-6.98, -0.98) * mm, "end": v(-7.1, -1.06) * mm});
            skLineSegment(sketch, "E322", {"start": v(-7.1, -1.06) * mm, "end": v(-7.24, -1.16) * mm});
            skLineSegment(sketch, "E323", {"start": v(-7.24, -1.16) * mm, "end": v(-7.35, -1.25) * mm});
            skLineSegment(sketch, "E324", {"start": v(-7.35, -1.25) * mm, "end": v(-7.47, -1.36) * mm});
            skLineSegment(sketch, "E325", {"start": v(-7.47, -1.36) * mm, "end": v(-7.57, -1.47) * mm});
            skLineSegment(sketch, "E326", {"start": v(-7.57, -1.47) * mm, "end": v(-7.67, -1.6) * mm});
            skLineSegment(sketch, "E327", {"start": v(-7.67, -1.6) * mm, "end": v(-7.75, -1.72) * mm});
            skLineSegment(sketch, "E328", {"start": v(-7.75, -1.72) * mm, "end": v(-7.83, -1.86) * mm});
            skLineSegment(sketch, "E329", {"start": v(-7.83, -1.86) * mm, "end": v(-7.9, -2) * mm});
            skLineSegment(sketch, "E330", {"start": v(-7.9, -2) * mm, "end": v(-7.77, -2.07) * mm});
            skLineSegment(sketch, "E331", {"start": v(-7.77, -2.07) * mm, "end": v(-7.63, -2.14) * mm});
            skLineSegment(sketch, "E332", {"start": v(-7.63, -2.14) * mm, "end": v(-7.48, -2.2) * mm});
            skLineSegment(sketch, "E333", {"start": v(-7.48, -2.2) * mm, "end": v(-7.34, -2.25) * mm});
            skLineSegment(sketch, "E334", {"start": v(-7.34, -2.25) * mm, "end": v(-7.19, -2.3) * mm});
            skLineSegment(sketch, "E335", {"start": v(-7.19, -2.3) * mm, "end": v(-7.04, -2.32) * mm});
            skLineSegment(sketch, "E336", {"start": v(-7.04, -2.32) * mm, "end": v(-6.88, -2.34) * mm});
            skLineSegment(sketch, "E337", {"start": v(-6.88, -2.34) * mm, "end": v(-6.73, -2.35) * mm});
            skLineSegment(sketch, "E338", {"start": v(-6.73, -2.35) * mm, "end": v(-6.57, -2.35) * mm});
            skLineSegment(sketch, "E339", {"start": v(-6.57, -2.35) * mm, "end": v(-6.42, -2.34) * mm});
            skLineSegment(sketch, "E340", {"start": v(-6.42, -2.34) * mm, "end": v(-6.26, -2.31) * mm});
            skLineSegment(sketch, "E341", {"start": v(-6.26, -2.31) * mm, "end": v(-6.12, -2.28) * mm});
            skLineSegment(sketch, "E342", {"start": v(-6.12, -2.28) * mm, "end": v(-5.97, -2.22) * mm});
            skLineSegment(sketch, "E343", {"start": v(-5.97, -2.22) * mm, "end": v(-5.83, -2.15) * mm});
            skLineSegment(sketch, "E344", {"start": v(-5.83, -2.15) * mm, "end": v(-5.69, -2.09) * mm});
            skLineSegment(sketch, "E345", {"start": v(-5.69, -2.09) * mm, "end": v(-5.54, -2.02) * mm});
            skLineSegment(sketch, "E346", {"start": v(-5.54, -2.02) * mm, "end": v(-5.4, -1.96) * mm});
            skLineSegment(sketch, "E347", {"start": v(-5.4, -1.96) * mm, "end": v(-5.26, -1.9) * mm});
            skLineSegment(sketch, "E348", {"start": v(-5.26, -1.9) * mm, "end": v(-5.12, -1.83) * mm});
            skLineSegment(sketch, "E349", {"start": v(-5.12, -1.83) * mm, "end": v(-4.97, -1.76) * mm});
            skLineSegment(sketch, "E350", {"start": v(-4.97, -1.76) * mm, "end": v(-4.83, -1.7) * mm});
            skLineSegment(sketch, "E351", {"start": v(-4.83, -1.7) * mm, "end": v(-4.69, -1.63) * mm});
            skLineSegment(sketch, "E352", {"start": v(-4.69, -1.63) * mm, "end": v(-4.6, -1.77) * mm});
            skLineSegment(sketch, "E353", {"start": v(-4.6, -1.77) * mm, "end": v(-4.51, -1.9) * mm});
            skLineSegment(sketch, "E354", {"start": v(-4.51, -1.9) * mm, "end": v(-4.43, -2.04) * mm});
            skLineSegment(sketch, "E355", {"start": v(-4.43, -2.04) * mm, "end": v(-4.34, -2.17) * mm});
            skLineSegment(sketch, "E356", {"start": v(-4.34, -2.17) * mm, "end": v(-4.26, -2.3) * mm});
            skLineSegment(sketch, "E357", {"start": v(-4.26, -2.3) * mm, "end": v(-4.17, -2.44) * mm});
            skLineSegment(sketch, "E358", {"start": v(-4.17, -2.44) * mm, "end": v(-4.08, -2.57) * mm});
            skLineSegment(sketch, "E359", {"start": v(-4.08, -2.57) * mm, "end": v(-4.2, -2.68) * mm});
            skLineSegment(sketch, "E360", {"start": v(-4.2, -2.68) * mm, "end": v(-4.32, -2.78) * mm});
            skLineSegment(sketch, "E361", {"start": v(-4.32, -2.78) * mm, "end": v(-4.44, -2.88) * mm});
            skLineSegment(sketch, "E362", {"start": v(-4.44, -2.88) * mm, "end": v(-4.56, -2.98) * mm});
            skLineSegment(sketch, "E363", {"start": v(-4.56, -2.98) * mm, "end": v(-4.68, -3.09) * mm});
            skLineSegment(sketch, "E364", {"start": v(-4.68, -3.09) * mm, "end": v(-4.8, -3.2) * mm});
            skLineSegment(sketch, "E365", {"start": v(-4.8, -3.2) * mm, "end": v(-4.91, -3.3) * mm});
            skLineSegment(sketch, "E366", {"start": v(-4.91, -3.3) * mm, "end": v(-5.03, -3.4) * mm});
            skLineSegment(sketch, "E367", {"start": v(-5.03, -3.4) * mm, "end": v(-5.15, -3.5) * mm});
            skLineSegment(sketch, "E368", {"start": v(-5.15, -3.5) * mm, "end": v(-5.27, -3.6) * mm});
            skLineSegment(sketch, "E369", {"start": v(-5.27, -3.6) * mm, "end": v(-5.36, -3.73) * mm});
            skLineSegment(sketch, "E370", {"start": v(-5.36, -3.73) * mm, "end": v(-5.44, -3.86) * mm});
            skLineSegment(sketch, "E371", {"start": v(-5.44, -3.86) * mm, "end": v(-5.52, -4) * mm});
            skLineSegment(sketch, "E372", {"start": v(-5.52, -4) * mm, "end": v(-5.58, -4.13) * mm});
            skLineSegment(sketch, "E373", {"start": v(-5.58, -4.13) * mm, "end": v(-5.64, -4.28) * mm});
            skLineSegment(sketch, "E374", {"start": v(-5.64, -4.28) * mm, "end": v(-5.69, -4.43) * mm});
            skLineSegment(sketch, "E375", {"start": v(-5.69, -4.43) * mm, "end": v(-5.72, -4.58) * mm});
            skLineSegment(sketch, "E376", {"start": v(-5.72, -4.58) * mm, "end": v(-5.75, -4.73) * mm});
            skLineSegment(sketch, "E377", {"start": v(-5.75, -4.73) * mm, "end": v(-5.76, -4.89) * mm});
            skLineSegment(sketch, "E378", {"start": v(-5.76, -4.89) * mm, "end": v(-5.77, -5.04) * mm});
            skLineSegment(sketch, "E379", {"start": v(-5.77, -5.04) * mm, "end": v(-5.76, -5.2) * mm});
            skLineSegment(sketch, "E380", {"start": v(-5.76, -5.2) * mm, "end": v(-5.75, -5.35) * mm});
            skLineSegment(sketch, "E381", {"start": v(-5.75, -5.35) * mm, "end": v(-5.59, -5.34) * mm});
            skLineSegment(sketch, "E382", {"start": v(-5.59, -5.34) * mm, "end": v(-5.44, -5.33) * mm});
            skLineSegment(sketch, "E383", {"start": v(-5.44, -5.33) * mm, "end": v(-5.28, -5.3) * mm});
            skLineSegment(sketch, "E384", {"start": v(-5.28, -5.3) * mm, "end": v(-5.14, -5.26) * mm});
            skLineSegment(sketch, "E385", {"start": v(-5.14, -5.26) * mm, "end": v(-4.98, -5.21) * mm});
            skLineSegment(sketch, "E386", {"start": v(-4.98, -5.21) * mm, "end": v(-4.84, -5.16) * mm});
            skLineSegment(sketch, "E387", {"start": v(-4.84, -5.16) * mm, "end": v(-4.7, -5.09) * mm});
            skLineSegment(sketch, "E388", {"start": v(-4.7, -5.09) * mm, "end": v(-4.57, -5.01) * mm});
            skLineSegment(sketch, "E389", {"start": v(-4.57, -5.01) * mm, "end": v(-4.43, -4.93) * mm});
            skLineSegment(sketch, "E390", {"start": v(-4.43, -4.93) * mm, "end": v(-4.31, -4.84) * mm});
            skLineSegment(sketch, "E391", {"start": v(-4.31, -4.84) * mm, "end": v(-4.2, -4.73) * mm});
            skLineSegment(sketch, "E392", {"start": v(-4.2, -4.73) * mm, "end": v(-4.09, -4.63) * mm});
            skLineSegment(sketch, "E393", {"start": v(-4.09, -4.63) * mm, "end": v(-4, -4.5) * mm});
            skLineSegment(sketch, "E394", {"start": v(-4, -4.5) * mm, "end": v(-3.92, -4.36) * mm});
            skLineSegment(sketch, "E395", {"start": v(-3.92, -4.36) * mm, "end": v(-3.83, -4.23) * mm});
            skLineSegment(sketch, "E396", {"start": v(-3.83, -4.23) * mm, "end": v(-3.75, -4.1) * mm});
            skLineSegment(sketch, "E397", {"start": v(-3.75, -4.1) * mm, "end": v(-3.66, -3.97) * mm});
            skLineSegment(sketch, "E398", {"start": v(-3.66, -3.97) * mm, "end": v(-3.58, -3.83) * mm});
            skLineSegment(sketch, "E399", {"start": v(-3.58, -3.83) * mm, "end": v(-3.5, -3.7) * mm});
            skLineSegment(sketch, "E400", {"start": v(-3.5, -3.7) * mm, "end": v(-3.4, -3.57) * mm});
            skLineSegment(sketch, "E401", {"start": v(-3.4, -3.57) * mm, "end": v(-3.32, -3.44) * mm});
            skLineSegment(sketch, "E402", {"start": v(-3.32, -3.44) * mm, "end": v(-3.24, -3.3) * mm});
            skLineSegment(sketch, "E403", {"start": v(-3.24, -3.3) * mm, "end": v(-3.1, -3.37) * mm});
            skLineSegment(sketch, "E404", {"start": v(-3.1, -3.37) * mm, "end": v(-2.95, -3.44) * mm});
            skLineSegment(sketch, "E405", {"start": v(-2.95, -3.44) * mm, "end": v(-2.8, -3.5) * mm});
            skLineSegment(sketch, "E406", {"start": v(-2.8, -3.5) * mm, "end": v(-2.66, -3.57) * mm});
            skLineSegment(sketch, "E407", {"start": v(-2.66, -3.57) * mm, "end": v(-2.51, -3.64) * mm});
            skLineSegment(sketch, "E408", {"start": v(-2.51, -3.64) * mm, "end": v(-2.37, -3.7) * mm});
            skLineSegment(sketch, "E409", {"start": v(-2.37, -3.7) * mm, "end": v(-2.22, -3.77) * mm});
            skLineSegment(sketch, "E410", {"start": v(-2.22, -3.77) * mm, "end": v(-2.26, -3.92) * mm});
            skLineSegment(sketch, "E411", {"start": v(-2.26, -3.92) * mm, "end": v(-2.3, -4.07) * mm});
            skLineSegment(sketch, "E412", {"start": v(-2.3, -4.07) * mm, "end": v(-2.35, -4.22) * mm});
            skLineSegment(sketch, "E413", {"start": v(-2.35, -4.22) * mm, "end": v(-2.4, -4.37) * mm});
            skLineSegment(sketch, "E414", {"start": v(-2.4, -4.37) * mm, "end": v(-2.44, -4.52) * mm});
            skLineSegment(sketch, "E415", {"start": v(-2.44, -4.52) * mm, "end": v(-2.48, -4.67) * mm});
            skLineSegment(sketch, "E416", {"start": v(-2.48, -4.67) * mm, "end": v(-2.53, -4.83) * mm});
            skLineSegment(sketch, "E417", {"start": v(-2.53, -4.83) * mm, "end": v(-2.57, -4.98) * mm});
            skLineSegment(sketch, "E418", {"start": v(-2.57, -4.98) * mm, "end": v(-2.62, -5.13) * mm});
            skLineSegment(sketch, "E419", {"start": v(-2.62, -5.13) * mm, "end": v(-2.66, -5.28) * mm});
            skLineSegment(sketch, "E420", {"start": v(-2.66, -5.28) * mm, "end": v(-2.67, -5.44) * mm});
            skLineSegment(sketch, "E421", {"start": v(-2.67, -5.44) * mm, "end": v(-2.67, -5.59) * mm});
            skLineSegment(sketch, "E422", {"start": v(-2.67, -5.59) * mm, "end": v(-2.66, -5.75) * mm});
            skLineSegment(sketch, "E423", {"start": v(-2.66, -5.75) * mm, "end": v(-2.64, -5.9) * mm});
            skLineSegment(sketch, "E424", {"start": v(-2.64, -5.9) * mm, "end": v(-2.6, -6.05) * mm});
            skLineSegment(sketch, "E425", {"start": v(-2.6, -6.05) * mm, "end": v(-2.57, -6.2) * mm});
            skLineSegment(sketch, "E426", {"start": v(-2.57, -6.2) * mm, "end": v(-2.51, -6.35) * mm});
            skLineSegment(sketch, "E427", {"start": v(-2.51, -6.35) * mm, "end": v(-2.45, -6.49) * mm});
            skLineSegment(sketch, "E428", {"start": v(-2.45, -6.49) * mm, "end": v(-2.38, -6.63) * mm});
            skLineSegment(sketch, "E429", {"start": v(-2.38, -6.63) * mm, "end": v(-2.3, -6.76) * mm});
            skLineSegment(sketch, "E430", {"start": v(-2.3, -6.76) * mm, "end": v(-2.21, -6.89) * mm});
            skLineSegment(sketch, "E431", {"start": v(-2.21, -6.89) * mm, "end": v(-2.12, -7) * mm});
            skLineSegment(sketch, "E432", {"start": v(-2.12, -7) * mm, "end": v(-1.99, -6.91) * mm});
            skLineSegment(sketch, "E433", {"start": v(-1.99, -6.91) * mm, "end": v(-1.87, -6.82) * mm});
            skLineSegment(sketch, "E434", {"start": v(-1.87, -6.82) * mm, "end": v(-1.76, -6.7) * mm});
            skLineSegment(sketch, "E435", {"start": v(-1.76, -6.7) * mm, "end": v(-1.65, -6.6) * mm});
            skLineSegment(sketch, "E436", {"start": v(-1.65, -6.6) * mm, "end": v(-1.55, -6.48) * mm});
            skLineSegment(sketch, "E437", {"start": v(-1.55, -6.48) * mm, "end": v(-1.46, -6.36) * mm});
            skLineSegment(sketch, "E438", {"start": v(-1.46, -6.36) * mm, "end": v(-1.38, -6.22) * mm});
            skLineSegment(sketch, "E439", {"start": v(-1.38, -6.22) * mm, "end": v(-1.3, -6.09) * mm});
            skLineSegment(sketch, "E440", {"start": v(-1.3, -6.09) * mm, "end": v(-1.24, -5.94) * mm});
            skLineSegment(sketch, "E441", {"start": v(-1.24, -5.94) * mm, "end": v(-1.2, -5.8) * mm});
            skLineSegment(sketch, "E442", {"start": v(-1.2, -5.8) * mm, "end": v(-1.15, -5.65) * mm});
            skLineSegment(sketch, "E443", {"start": v(-1.15, -5.65) * mm, "end": v(-1.11, -5.5) * mm});
            skLineSegment(sketch, "E444", {"start": v(-1.11, -5.5) * mm, "end": v(-1.11, -5.34) * mm});
            skLineSegment(sketch, "E445", {"start": v(-1.11, -5.34) * mm, "end": v(-1.11, -5.19) * mm});
            skLineSegment(sketch, "E446", {"start": v(-1.11, -5.19) * mm, "end": v(-1.11, -5.03) * mm});
            skLineSegment(sketch, "E447", {"start": v(-1.11, -5.03) * mm, "end": v(-1.11, -4.87) * mm});
            skLineSegment(sketch, "E448", {"start": v(-1.11, -4.87) * mm, "end": v(-1.11, -4.71) * mm});
            skLineSegment(sketch, "E449", {"start": v(-1.11, -4.71) * mm, "end": v(-1.11, -4.56) * mm});
            skLineSegment(sketch, "E450", {"start": v(-1.11, -4.56) * mm, "end": v(-1.11, -4.4) * mm});
            skLineSegment(sketch, "E451", {"start": v(-1.11, -4.4) * mm, "end": v(-1.11, -4.24) * mm});
            skLineSegment(sketch, "E452", {"start": v(-1.11, -4.24) * mm, "end": v(-1.11, -4.09) * mm});
            skLineSegment(sketch, "E453", {"start": v(-1.11, -4.09) * mm, "end": v(-1.11, -3.93) * mm});
            skLineSegment(sketch, "E454", {"start": v(-1.11, -3.93) * mm, "end": v(-0.95, -3.9) * mm});
            skLineSegment(sketch, "E455", {"start": v(-0.95, -3.9) * mm, "end": v(-0.8, -3.88) * mm});
            skLineSegment(sketch, "E456", {"start": v(-0.8, -3.88) * mm, "end": v(-0.64, -3.86) * mm});
            skLineSegment(sketch, "E457", {"start": v(-0.64, -3.86) * mm, "end": v(-0.48, -3.84) * mm});
            skLineSegment(sketch, "E458", {"start": v(-0.48, -3.84) * mm, "end": v(-0.32, -3.82) * mm});
            skLineSegment(sketch, "E459", {"start": v(-0.32, -3.82) * mm, "end": v(-0.16, -3.8) * mm});
            skLineSegment(sketch, "E460", {"start": v(-0.16, -3.8) * mm, "end": v(0, -3.77) * mm});
            skLineSegment(sketch, "E461", {"start": v(0, -3.77) * mm, "end": v(0.04, -3.92) * mm});
            skLineSegment(sketch, "E462", {"start": v(0.04, -3.92) * mm, "end": v(0.08, -4.07) * mm});
            skLineSegment(sketch, "E463", {"start": v(0.08, -4.07) * mm, "end": v(0.13, -4.22) * mm});
            skLineSegment(sketch, "E464", {"start": v(0.13, -4.22) * mm, "end": v(0.17, -4.37) * mm});
            skLineSegment(sketch, "E465", {"start": v(0.17, -4.37) * mm, "end": v(0.22, -4.52) * mm});
            skLineSegment(sketch, "E466", {"start": v(0.22, -4.52) * mm, "end": v(0.26, -4.67) * mm});
            skLineSegment(sketch, "E467", {"start": v(0.26, -4.67) * mm, "end": v(0.3, -4.83) * mm});
            skLineSegment(sketch, "E468", {"start": v(0.3, -4.83) * mm, "end": v(0.35, -4.98) * mm});
            skLineSegment(sketch, "E469", {"start": v(0.35, -4.98) * mm, "end": v(0.4, -5.13) * mm});
            skLineSegment(sketch, "E470", {"start": v(0.4, -5.13) * mm, "end": v(0.44, -5.28) * mm});
            skLineSegment(sketch, "E471", {"start": v(0.44, -5.28) * mm, "end": v(0.52, -5.42) * mm});
            skLineSegment(sketch, "E472", {"start": v(0.52, -5.42) * mm, "end": v(0.6, -5.54) * mm});
            skLineSegment(sketch, "E473", {"start": v(0.6, -5.54) * mm, "end": v(0.7, -5.67) * mm});
            skLineSegment(sketch, "E474", {"start": v(0.7, -5.67) * mm, "end": v(0.8, -5.78) * mm});
            skLineSegment(sketch, "E475", {"start": v(0.8, -5.78) * mm, "end": v(0.9, -5.9) * mm});
            skLineSegment(sketch, "E476", {"start": v(0.9, -5.9) * mm, "end": v(1.01, -6) * mm});
            skLineSegment(sketch, "E477", {"start": v(1.01, -6) * mm, "end": v(1.14, -6.1) * mm});
            skLineSegment(sketch, "E478", {"start": v(1.14, -6.1) * mm, "end": v(1.27, -6.18) * mm});
            skLineSegment(sketch, "E479", {"start": v(1.27, -6.18) * mm, "end": v(1.4, -6.26) * mm});
            skLineSegment(sketch, "E480", {"start": v(1.4, -6.26) * mm, "end": v(1.54, -6.33) * mm});
            skLineSegment(sketch, "E481", {"start": v(1.54, -6.33) * mm, "end": v(1.69, -6.39) * mm});
            skLineSegment(sketch, "E482", {"start": v(1.69, -6.39) * mm, "end": v(1.83, -6.44) * mm});
            skLineSegment(sketch, "E483", {"start": v(1.83, -6.44) * mm, "end": v(1.89, -6.29) * mm});
            skLineSegment(sketch, "E484", {"start": v(1.89, -6.29) * mm, "end": v(1.93, -6.15) * mm});
            skLineSegment(sketch, "E485", {"start": v(1.93, -6.15) * mm, "end": v(1.97, -6) * mm});
            skLineSegment(sketch, "E486", {"start": v(1.97, -6) * mm, "end": v(2, -5.84) * mm});
            skLineSegment(sketch, "E487", {"start": v(2, -5.84) * mm, "end": v(2.02, -5.69) * mm});
            skLineSegment(sketch, "E488", {"start": v(2.02, -5.69) * mm, "end": v(2.03, -5.54) * mm});
            skLineSegment(sketch, "E489", {"start": v(2.03, -5.54) * mm, "end": v(2.02, -5.38) * mm});
            skLineSegment(sketch, "E490", {"start": v(2.02, -5.38) * mm, "end": v(2.01, -5.23) * mm});
            skLineSegment(sketch, "E491", {"start": v(2.01, -5.23) * mm, "end": v(1.99, -5.07) * mm});
            skLineSegment(sketch, "E492", {"start": v(1.99, -5.07) * mm, "end": v(1.96, -4.92) * mm});
            skLineSegment(sketch, "E493", {"start": v(1.96, -4.92) * mm, "end": v(1.91, -4.77) * mm});
            skLineSegment(sketch, "E494", {"start": v(1.91, -4.77) * mm, "end": v(1.86, -4.63) * mm});
            skLineSegment(sketch, "E495", {"start": v(1.86, -4.63) * mm, "end": v(1.78, -4.5) * mm});
            skLineSegment(sketch, "E496", {"start": v(1.78, -4.5) * mm, "end": v(1.7, -4.36) * mm});
            skLineSegment(sketch, "E497", {"start": v(1.7, -4.36) * mm, "end": v(1.6, -4.23) * mm});
            skLineSegment(sketch, "E498", {"start": v(1.6, -4.23) * mm, "end": v(1.52, -4.1) * mm});
            skLineSegment(sketch, "E499", {"start": v(1.52, -4.1) * mm, "end": v(1.44, -3.97) * mm});
            skLineSegment(sketch, "E500", {"start": v(1.44, -3.97) * mm, "end": v(1.35, -3.83) * mm});
            skLineSegment(sketch, "E501", {"start": v(1.35, -3.83) * mm, "end": v(1.27, -3.7) * mm});
            skLineSegment(sketch, "E502", {"start": v(1.27, -3.7) * mm, "end": v(1.18, -3.57) * mm});
            skLineSegment(sketch, "E503", {"start": v(1.18, -3.57) * mm, "end": v(1.1, -3.44) * mm});
            skLineSegment(sketch, "E504", {"start": v(1.1, -3.44) * mm, "end": v(1.01, -3.3) * mm});
            skLineSegment(sketch, "E505", {"start": v(1.01, -3.3) * mm, "end": v(1.13, -3.2) * mm});
            skLineSegment(sketch, "E506", {"start": v(1.13, -3.2) * mm, "end": v(1.25, -3.1) * mm});
            skLineSegment(sketch, "E507", {"start": v(1.25, -3.1) * mm, "end": v(1.37, -3) * mm});
            skLineSegment(sketch, "E508", {"start": v(1.37, -3) * mm, "end": v(1.5, -2.89) * mm});
            skLineSegment(sketch, "E509", {"start": v(1.5, -2.89) * mm, "end": v(1.62, -2.78) * mm});
            skLineSegment(sketch, "E510", {"start": v(1.62, -2.78) * mm, "end": v(1.74, -2.68) * mm});
            skLineSegment(sketch, "E511", {"start": v(1.74, -2.68) * mm, "end": v(1.86, -2.57) * mm});
            skLineSegment(sketch, "E512", {"start": v(1.86, -2.57) * mm, "end": v(1.98, -2.68) * mm});
            skLineSegment(sketch, "E513", {"start": v(1.98, -2.68) * mm, "end": v(2.1, -2.78) * mm});
            skLineSegment(sketch, "E514", {"start": v(2.1, -2.78) * mm, "end": v(2.21, -2.88) * mm});
            skLineSegment(sketch, "E515", {"start": v(2.21, -2.88) * mm, "end": v(2.33, -2.98) * mm});
            skLineSegment(sketch, "E516", {"start": v(2.33, -2.98) * mm, "end": v(2.45, -3.09) * mm});
            skLineSegment(sketch, "E517", {"start": v(2.45, -3.09) * mm, "end": v(2.57, -3.2) * mm});
            skLineSegment(sketch, "E518", {"start": v(2.57, -3.2) * mm, "end": v(2.69, -3.3) * mm});
            skLineSegment(sketch, "E519", {"start": v(2.69, -3.3) * mm, "end": v(2.8, -3.4) * mm});
            skLineSegment(sketch, "E520", {"start": v(2.8, -3.4) * mm, "end": v(2.93, -3.5) * mm});
            skLineSegment(sketch, "E521", {"start": v(2.93, -3.5) * mm, "end": v(3.04, -3.6) * mm});
            skLineSegment(sketch, "E522", {"start": v(3.04, -3.6) * mm, "end": v(3.19, -3.68) * mm});
            skLineSegment(sketch, "E523", {"start": v(3.19, -3.68) * mm, "end": v(3.32, -3.74) * mm});
            skLineSegment(sketch, "E524", {"start": v(3.32, -3.74) * mm, "end": v(3.47, -3.8) * mm});
            skLineSegment(sketch, "E525", {"start": v(3.47, -3.8) * mm, "end": v(3.62, -3.84) * mm});
            skLineSegment(sketch, "E526", {"start": v(3.62, -3.84) * mm, "end": v(3.77, -3.87) * mm});
            skLineSegment(sketch, "E527", {"start": v(3.77, -3.87) * mm, "end": v(3.92, -3.9) * mm});
            skLineSegment(sketch, "E528", {"start": v(3.92, -3.9) * mm, "end": v(4.08, -3.9) * mm});
            skLineSegment(sketch, "E529", {"start": v(4.08, -3.9) * mm, "end": v(4.23, -3.91) * mm});
            skLineSegment(sketch, "E530", {"start": v(4.23, -3.91) * mm, "end": v(4.39, -3.9) * mm});
            skLineSegment(sketch, "E531", {"start": v(4.39, -3.9) * mm, "end": v(4.54, -3.9) * mm});
            skLineSegment(sketch, "E532", {"start": v(4.54, -3.9) * mm, "end": v(4.7, -3.86) * mm});
            skLineSegment(sketch, "E533", {"start": v(4.7, -3.86) * mm, "end": v(4.84, -3.83) * mm});
            skLineSegment(sketch, "E534", {"start": v(4.84, -3.83) * mm, "end": v(4.81, -3.67) * mm});
            skLineSegment(sketch, "E535", {"start": v(4.81, -3.67) * mm, "end": v(4.77, -3.52) * mm});
            skLineSegment(sketch, "E536", {"start": v(4.77, -3.52) * mm, "end": v(4.72, -3.37) * mm});
            skLineSegment(sketch, "E537", {"start": v(4.72, -3.37) * mm, "end": v(4.67, -3.23) * mm});
            skLineSegment(sketch, "E538", {"start": v(4.67, -3.23) * mm, "end": v(4.6, -3.1) * mm});
            skLineSegment(sketch, "E539", {"start": v(4.6, -3.1) * mm, "end": v(4.52, -2.96) * mm});
            skLineSegment(sketch, "E540", {"start": v(4.52, -2.96) * mm, "end": v(4.43, -2.83) * mm});
            skLineSegment(sketch, "E541", {"start": v(4.43, -2.83) * mm, "end": v(4.34, -2.7) * mm});
            skLineSegment(sketch, "E542", {"start": v(4.34, -2.7) * mm, "end": v(4.24, -2.59) * mm});
            skLineSegment(sketch, "E543", {"start": v(4.24, -2.59) * mm, "end": v(4.13, -2.48) * mm});
            skLineSegment(sketch, "E544", {"start": v(4.13, -2.48) * mm, "end": v(4, -2.38) * mm});
            skLineSegment(sketch, "E545", {"start": v(4, -2.38) * mm, "end": v(3.9, -2.28) * mm});
            skLineSegment(sketch, "E546", {"start": v(3.9, -2.28) * mm, "end": v(3.75, -2.22) * mm});
            skLineSegment(sketch, "E547", {"start": v(3.75, -2.22) * mm, "end": v(3.6, -2.15) * mm});
            skLineSegment(sketch, "E548", {"start": v(3.6, -2.15) * mm, "end": v(3.46, -2.09) * mm});
            skLineSegment(sketch, "E549", {"start": v(3.46, -2.09) * mm, "end": v(3.32, -2.02) * mm});
            skLineSegment(sketch, "E550", {"start": v(3.32, -2.02) * mm, "end": v(3.18, -1.96) * mm});
            skLineSegment(sketch, "E551", {"start": v(3.18, -1.96) * mm, "end": v(3.03, -1.9) * mm});
            skLineSegment(sketch, "E552", {"start": v(3.03, -1.9) * mm, "end": v(2.9, -1.83) * mm});
            skLineSegment(sketch, "E553", {"start": v(2.9, -1.83) * mm, "end": v(2.75, -1.76) * mm});
            skLineSegment(sketch, "E554", {"start": v(2.75, -1.76) * mm, "end": v(2.6, -1.7) * mm});
            skLineSegment(sketch, "E555", {"start": v(2.6, -1.7) * mm, "end": v(2.46, -1.63) * mm});
            skLineSegment(sketch, "E556", {"start": v(2.46, -1.63) * mm, "end": v(2.5, -1.48) * mm});
            skLineSegment(sketch, "E557", {"start": v(2.5, -1.48) * mm, "end": v(2.55, -1.33) * mm});
            skLineSegment(sketch, "E558", {"start": v(2.55, -1.33) * mm, "end": v(2.6, -1.17) * mm});
            skLineSegment(sketch, "E559", {"start": v(2.6, -1.17) * mm, "end": v(2.64, -1.02) * mm});
            skLineSegment(sketch, "E560", {"start": v(2.64, -1.02) * mm, "end": v(2.69, -0.87) * mm});
            skLineSegment(sketch, "E561", {"start": v(2.69, -0.87) * mm, "end": v(2.73, -0.71) * mm});
            skLineSegment(sketch, "E562", {"start": v(2.73, -0.71) * mm, "end": v(2.78, -0.56) * mm});
            skPoint(sketch, "E563", {"position": v(-1.11, 0) * mm});
            skLineSegment(sketch, "E564", {"start": v(-1.11, 3) * mm, "end": v(-1.11, -2.5) * mm, "construction": true});
            skLineSegment(sketch, "E565", {"start": v(-2.77, -2.5) * mm, "end": v(0.55, -2.5) * mm});
            skCircle(sketch, "E566", {"center": v(-1.11, 0) * mm, "radius": 1.5 * mm});
            skCircle(sketch, "E567", {"center": v(-1.11, 0) * mm, "radius": 3 * mm});
            skSolve(sketch);
        }
        {
            var Q0;
            Q0=makeQuery(id+"F0.imprint","IMPRINT",FACE,{"disambiguationData":[TD([[makeQuery(id+"F0.imprint","IMPRINT",EDGE,{"derivedFrom":sQuery(id+"F0.wireOp",EDGE,"E0")}),1.0]])]});
            var Q1;
            {var subQ0=sQuery(id+"F0.wireOp",EDGE,"E565");Q1=makeQuery(id+"F0.imprint","IMPRINT",FACE,{"disambiguationData":[TD([[makeQuery(id+"F0.imprint","IMPRINT",EDGE,{"derivedFrom":subQ0}),-1.0]])]});}
            extrude(context, id + "F1", {"entities" : qUnion([Q0, Q1]), "depth" : 7 * mm});
        }
    });
